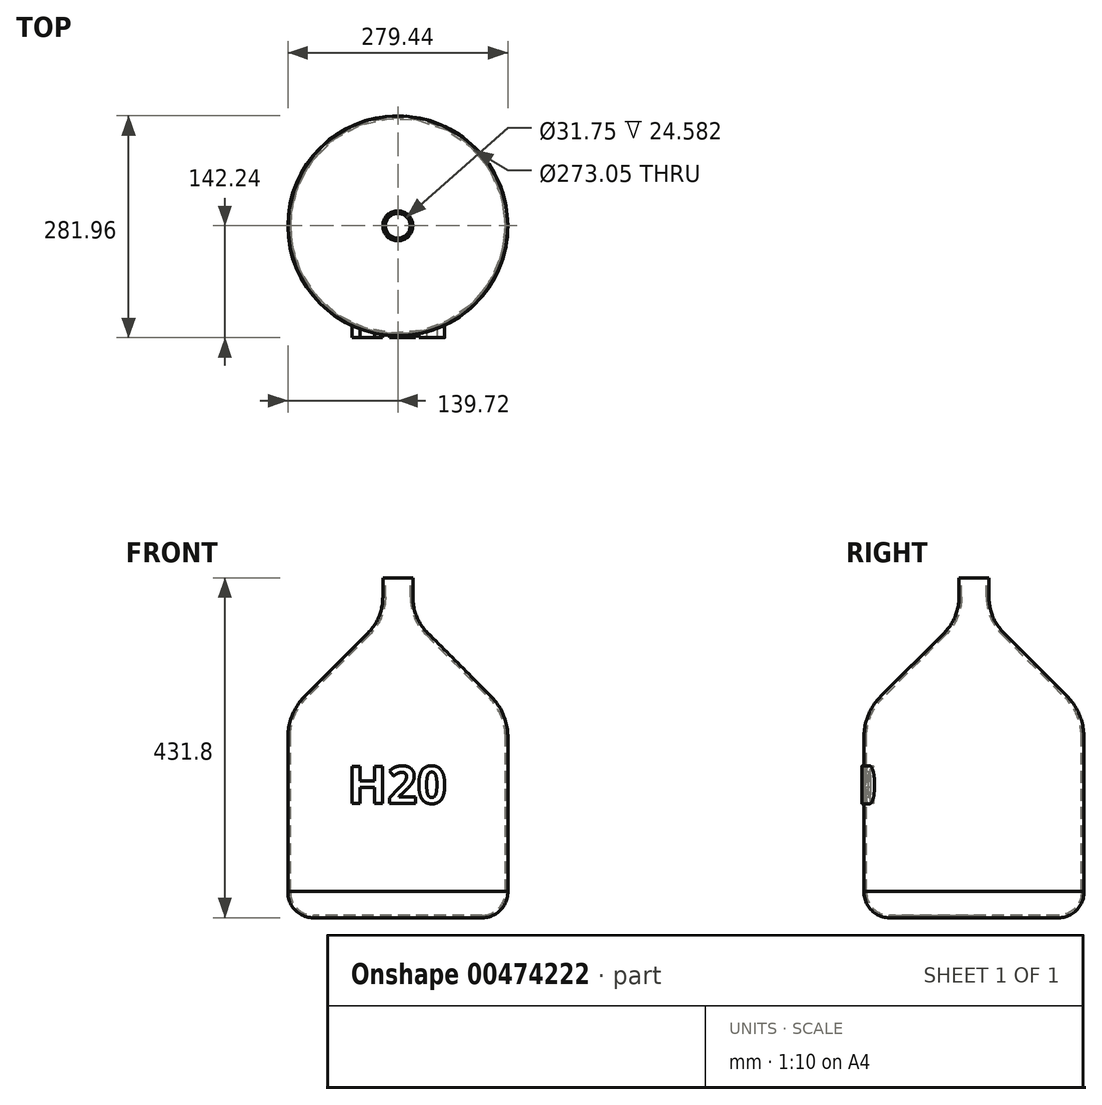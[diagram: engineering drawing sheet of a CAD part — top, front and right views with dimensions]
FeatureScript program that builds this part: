
annotation { "Feature Type Name" : "Feature", "Feature Type Description" : "" }
export const myFeature = defineFeature(function(context is Context, id is Id, definition is map)
    precondition{}
    {
        {
            var Q0;
            Q0=qCreatedBy(makeId("Front.planeOp"),FACE);
            var sketch = newSketch(context, id + "F0", { "sketchPlane" : qUnion([Q0])});
            skLineSegment(sketch, "E0", {"start": v(0, 0) * mm, "end": v(-107.21, 0) * mm});
            skArc(sketch, "E1", {"start": v(-107.21, 0) * mm, "mid": v(-130.6, 9.92) * mm, "end": v(-139.7, 33.63) * mm});
            skLineSegment(sketch, "E2", {"start": v(-139.7, 33.63) * mm, "end": v(-139.7, 229.3) * mm});
            skLineSegment(sketch, "E3", {"start": v(-19.05, 431.8) * mm, "end": v(0, 431.8) * mm});
            skLineSegment(sketch, "E4", {"start": v(0, 431.8) * mm, "end": v(0, 0) * mm});
            skLineSegment(sketch, "E5", {"start": v(-19.05, 431.8) * mm, "end": v(-19.05, 407.22) * mm});
            skArc(sketch, "E6", {"start": v(-19.05, 407.22) * mm, "mid": v(-23.93, 382.67) * mm, "end": v(-37.84, 361.85) * mm});
            skLineSegment(sketch, "E7", {"start": v(-37.84, 361.85) * mm, "end": v(-117.99, 281.7) * mm});
            skArc(sketch, "E8", {"start": v(-117.99, 281.7) * mm, "mid": v(-134.06, 257.66) * mm, "end": v(-139.7, 229.3) * mm});
            skSolve(sketch);
        }
        {
            var Q0;
            Q0=makeQuery(id+"F0.imprint","IMPRINT",FACE,{"disambiguationData":[TD([[makeQuery(id+"F0.imprint","IMPRINT",EDGE,{"derivedFrom":sQuery(id+"F0.wireOp",EDGE,"E0")}),-1.0]])]});
            var Q1;
            Q1=sQuery(id+"F0.wireOp",EDGE,"E4");
            revolve(context, id + "F1", {"entities" : qUnion([Q0]), "axis" : qUnion([Q1]), "revolveType" : RevolveType.FULL});
        }
        {
            var Q0;
            Q0=makeQuery(id+"F1.opRevolve","SWEPT_FACE",FACE,{"disambiguationData":[OSD([sQuery(id+"F0.wireOp",EDGE,"E3")])]});
            shell(context, id + "F2", {"entities" : qUnion([Q0]), "thickness" : 3.17 * mm});
        }
        {
            var Q0;
            Q0=qCreatedBy(makeId("Front.planeOp"),FACE);
            cPlane(context, id + "F3", {"entities" : qUnion([Q0]), "cplaneType" : CPlaneType.OFFSET, "offset" : 142.24 * mm, "width" : 152.4 * mm, "height" : 152.4 * mm});
        }
        {
            var Q0;
            Q0=qCreatedBy(id+"F3.planeOp",FACE);
            var sketch = newSketch(context, id + "F4", { "sketchPlane" : qUnion([Q0])});
            skText(sketch, "E9", { "text": "H20", "fontName": "OpenSans-Bold.ttf"});
            const initialGuessF4  = {"E9": [-0.06381, 0.14529, 1, 0, 0.04747]};
            skSetInitialGuess(sketch, initialGuessF4);
            skSolve(sketch);
        }
        {
            var Q0;
            Q0 = qSketchRegion(id + "F4", true);
            var Q1;
            Q1=makeQuery(id+"F1.opRevolve","SWEPT_FACE",FACE,{"disambiguationData":[OSD([sQuery(id+"F0.wireOp",EDGE,"E2")])]});
            extrude(context, id + "F5", {"entities" : qUnion([Q0]), "operationType" : NewBodyOperationType.ADD, "endBound" : BoundingType.UP_TO_SURFACE, "oppositeDirection" : true, "endBoundEntityFace" : qUnion([Q1]), "depth" : 25.4 * mm});
        }
    });
